# Revit family: Haworth_XSeries_ConvergentDTop
name_source: partatom
category: Furniture Systems
revit_build: Autodesk Revit 2018 (Build: 20170223_1515(x64)
units: mm (PartAtom-declared; Revit-internal decimal feet)

## family parameters
Always vertical = Yes
Cut with Voids When Loaded = No
OmniClass Number = 23.40.70.14.64.21
OmniClass Title = Systems Furniture
Part Type = Normal
Room Calculation Point = No
Round Connector Dimension = Use Diameter
Shared = No
Work Plane-Based = No

## types (3) — shared parameters
Actual Height = 29 1/8"
Actual Width = 72"
Assembly Code = E2020200
Column Support = Yes
Custom Size = No
Description = Haworth XSeries Convergent DTop
End Panel = Yes
Manufacturer = Haworth
Max. Depth = 48"
Max. Width = 72"
Min. Depth = 24"
Min. Width = 48"
Model = JDDL-xx72
Revision Number = 3
Size = Verify Final Dim. w/ Haworth
Standard Depths = 24, 30, 36 in.
Standard Widths = 48, 54, 60, 66, 72 in.
Sustainability Info = https://www.haworth.com
URL = http://www.haworth.com
URL - Product = https://www.haworth.com
Warranty = http://www.haworth.com
Width = 72"

## per-type parameters (varying)
| type | Actual Depth | Depth | Support Position |
| 30d 72w 29h | 30" | 30" | 15" |
| 24d 72w 29h | 24" | 24" | 12" |
| 36d 72w 29h | 36" | 36" | 18" |

## geometry (parser evidence)
native form markers: Sweep x3
no freeform markers — native parametric forms only
